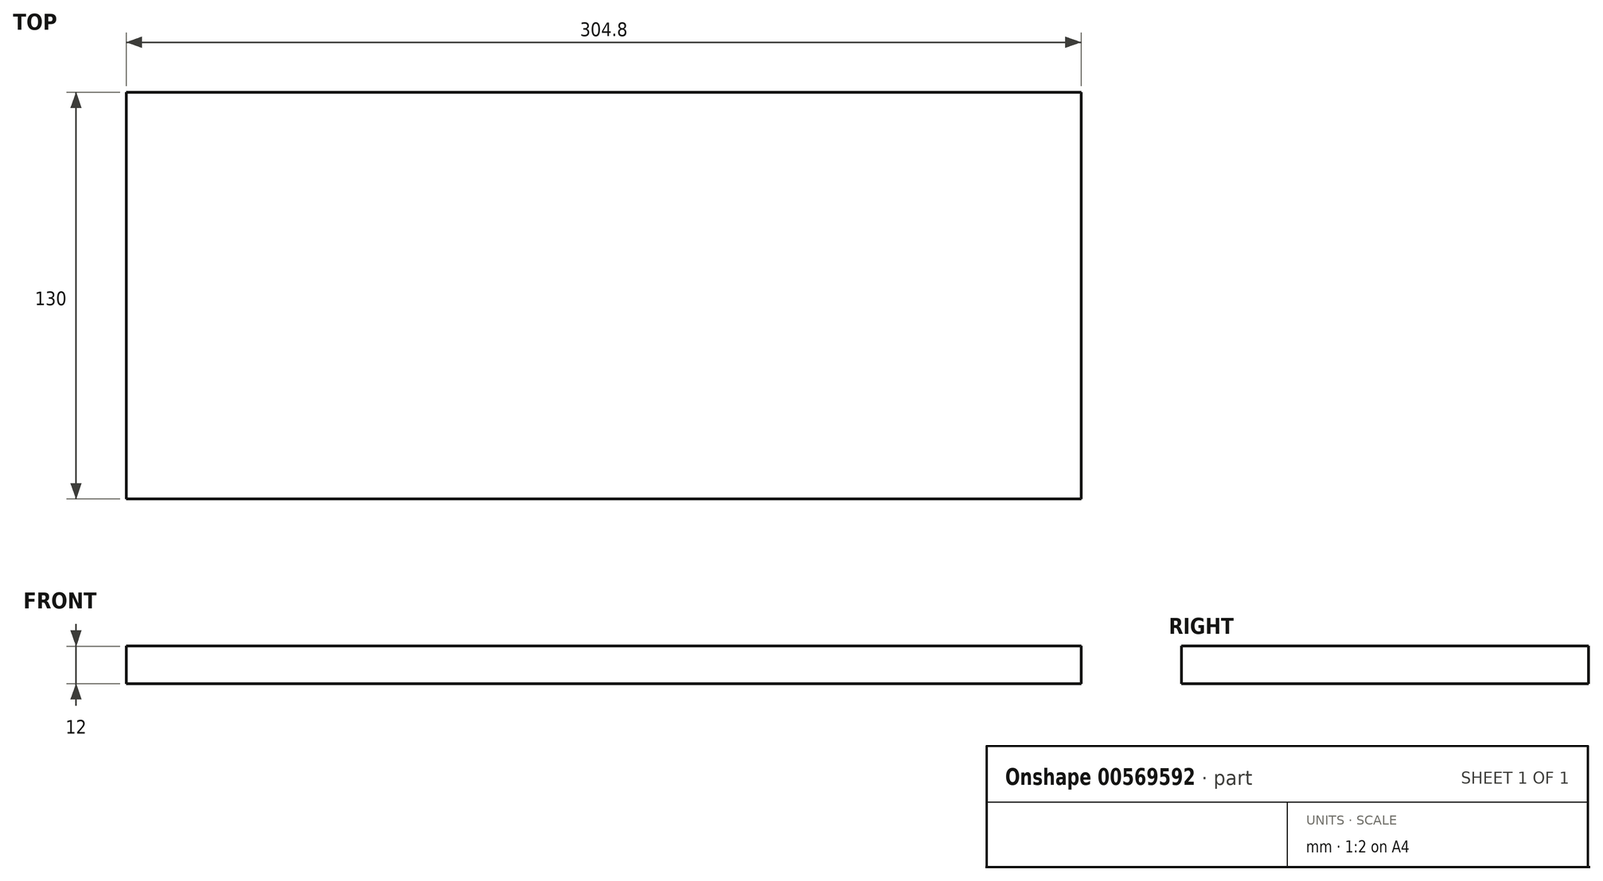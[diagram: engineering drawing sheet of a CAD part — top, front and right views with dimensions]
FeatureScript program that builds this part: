
annotation { "Feature Type Name" : "Feature", "Feature Type Description" : "" }
export const myFeature = defineFeature(function(context is Context, id is Id, definition is map)
    precondition{}
    {
        {
            var Q0;
            Q0=qCreatedBy(makeId("Front.planeOp"),FACE);
            var sketch = newSketch(context, id + "F0", { "sketchPlane" : qUnion([Q0])});
            skLineSegment(sketch, "E0.bottom", {"start": v(-151.91, -39.39) * mm, "end": v(152.89, -39.39) * mm});
            skLineSegment(sketch, "E0.top", {"start": v(-151.91, -51.39) * mm, "end": v(152.89, -51.39) * mm});
            skLineSegment(sketch, "E0.left", {"start": v(-151.91, -39.39) * mm, "end": v(-151.91, -51.39) * mm});
            skLineSegment(sketch, "E0.right", {"start": v(152.89, -39.39) * mm, "end": v(152.89, -51.39) * mm});
            skSolve(sketch);
        }
        {
            var Q0;
            Q0=makeQuery(id+"F0.imprint","IMPRINT",FACE,{"disambiguationData":[TD([[makeQuery(id+"F0.imprint","IMPRINT",EDGE,{"derivedFrom":sQuery(id+"F0.wireOp",EDGE,"E0.bottom")}),-1.0]])]});
            extrude(context, id + "F1", {"entities" : qUnion([Q0]), "depth" : 130 * mm, "offsetDistance" : 25.4 * mm});
        }
    });
